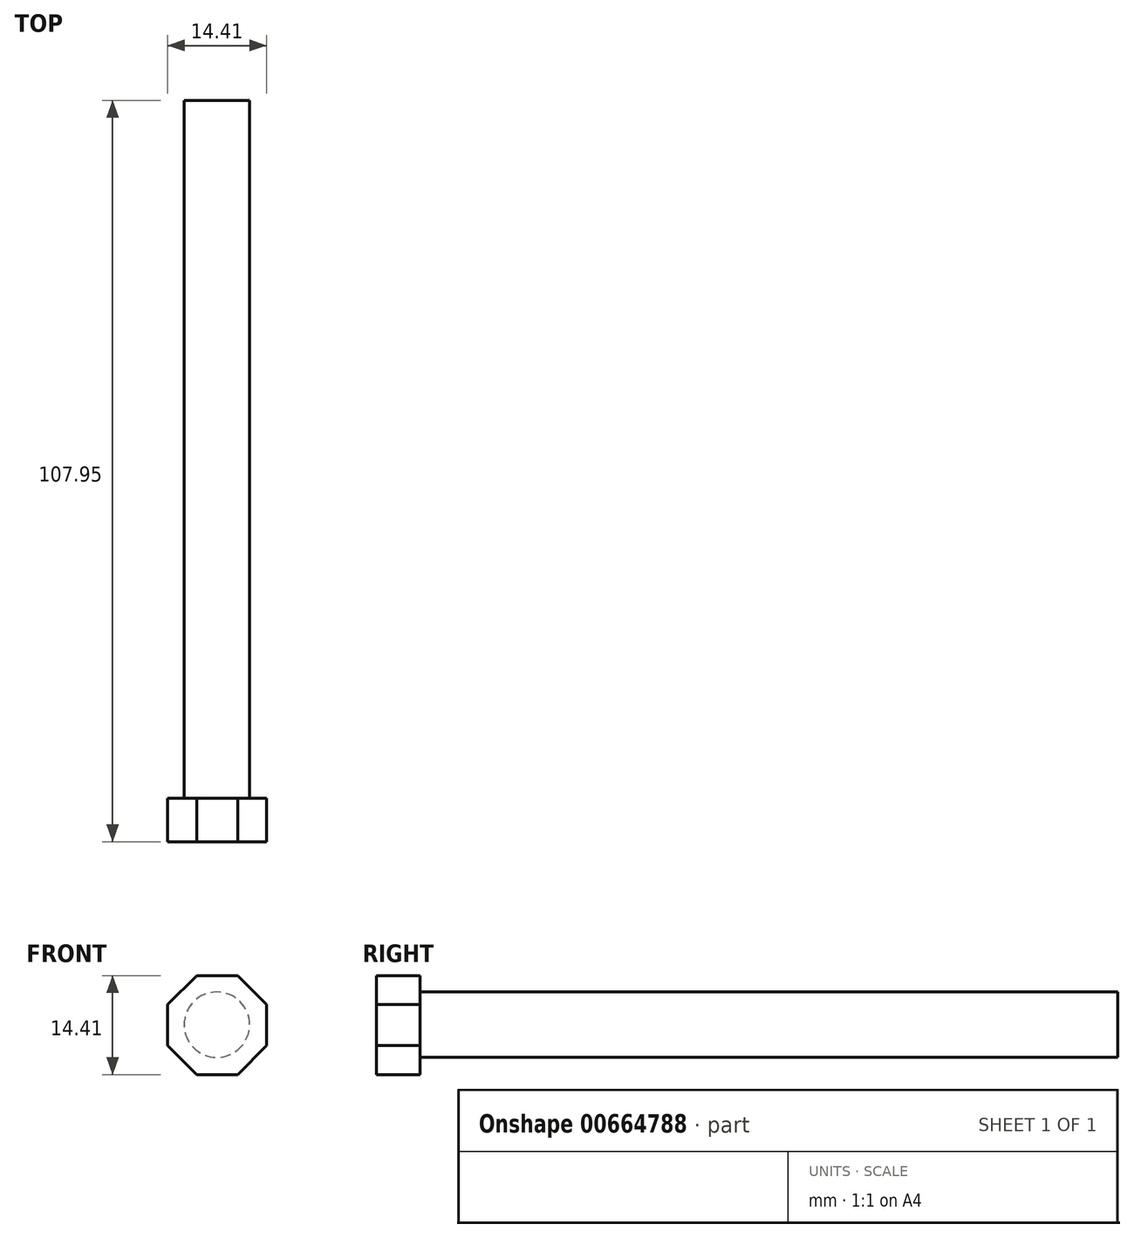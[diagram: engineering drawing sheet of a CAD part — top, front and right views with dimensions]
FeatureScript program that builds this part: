
annotation { "Feature Type Name" : "Feature", "Feature Type Description" : "" }
export const myFeature = defineFeature(function(context is Context, id is Id, definition is map)
    precondition{}
    {
        {
            var Q0;
            Q0=qCreatedBy(makeId("Front.planeOp"),FACE);
            var sketch = newSketch(context, id + "F0", { "sketchPlane" : qUnion([Q0])});
            skCircle(sketch, "E0", {"center": v(0, 0) * mm, "radius": 4.76 * mm});
            skSolve(sketch);
        }
        {
            var Q0;
            Q0 = qSketchRegion(id + "F0", true);
            extrude(context, id + "F1", {"entities" : qUnion([Q0]), "oppositeDirection" : true, "depth" : 101.6 * mm, "offsetDistance" : 25.4 * mm});
        }
        {
            var Q0;
            Q0=qCreatedBy(makeId("Front.planeOp"),FACE);
            var sketch = newSketch(context, id + "F2", { "sketchPlane" : qUnion([Q0])});
            skCircle(sketch, "E1.cCircle", {"center": v(0.03, -0.06) * mm, "radius": 7.2 * mm, "construction": true});
            skLineSegment(sketch, "E1.0", {"start": v(3.01, -7.26) * mm, "end": v(-2.96, -7.26) * mm});
            skLineSegment(sketch, "E1.1", {"start": v(-2.96, -7.26) * mm, "end": v(-7.18, -3.04) * mm});
            skLineSegment(sketch, "E1.2", {"start": v(-7.18, -3.04) * mm, "end": v(-7.18, 2.93) * mm});
            skLineSegment(sketch, "E1.3", {"start": v(-7.18, 2.93) * mm, "end": v(-2.96, 7.15) * mm});
            skLineSegment(sketch, "E1.4", {"start": v(-2.96, 7.15) * mm, "end": v(3.01, 7.15) * mm});
            skLineSegment(sketch, "E1.5", {"start": v(3.01, 7.15) * mm, "end": v(7.23, 2.93) * mm});
            skLineSegment(sketch, "E1.6", {"start": v(7.23, 2.93) * mm, "end": v(7.23, -3.04) * mm});
            skLineSegment(sketch, "E1.7", {"start": v(7.23, -3.04) * mm, "end": v(3.01, -7.26) * mm});
            skPoint(sketch, "E1.0.midPoint", {"position": v(0.03, -7.26) * mm});
            skSolve(sketch);
        }
        {
            var Q0;
            Q0 = qSketchRegion(id + "F2", true);
            extrude(context, id + "F3", {"entities" : qUnion([Q0]), "operationType" : NewBodyOperationType.ADD, "depth" : 6.35 * mm, "offsetDistance" : 25.4 * mm});
        }
    });
